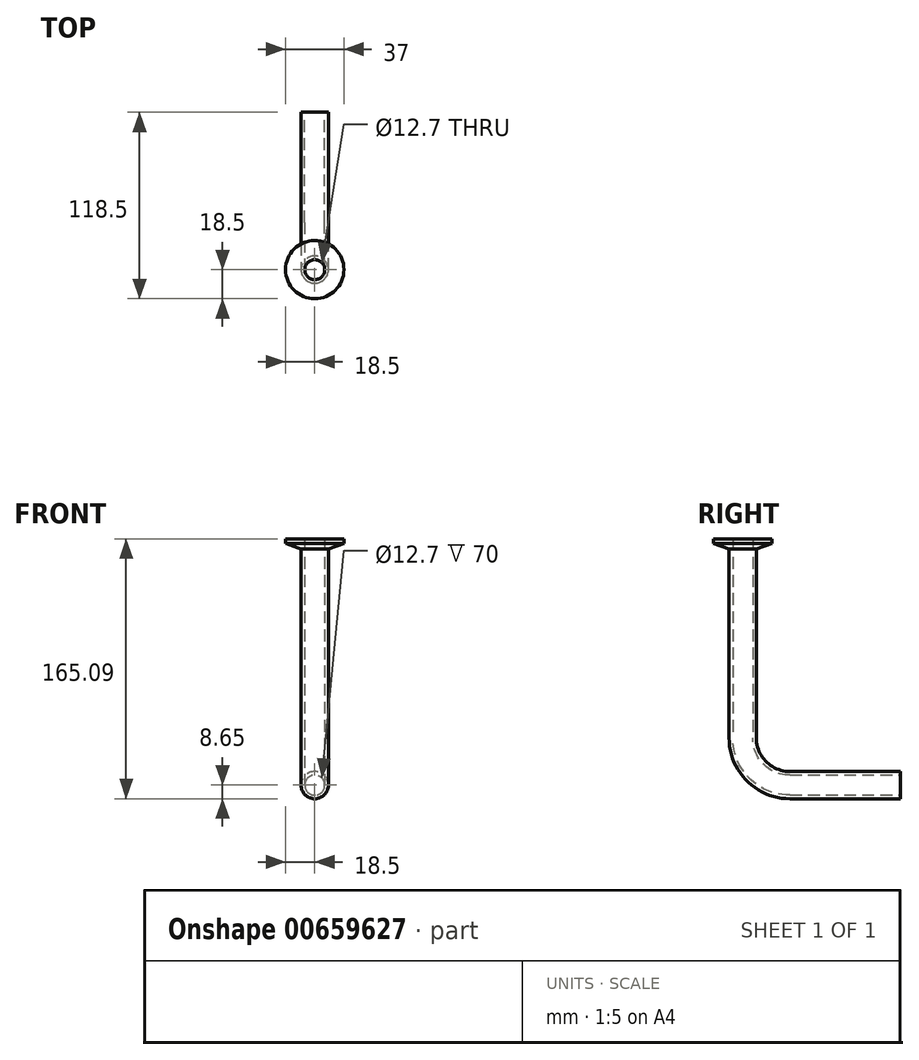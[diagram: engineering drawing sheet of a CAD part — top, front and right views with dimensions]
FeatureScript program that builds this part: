
annotation { "Feature Type Name" : "Feature", "Feature Type Description" : "" }
export const myFeature = defineFeature(function(context is Context, id is Id, definition is map)
    precondition{}
    {
        {
            var Q0;
            Q0=qCreatedBy(makeId("Front.planeOp"),FACE);
            var sketch = newSketch(context, id + "F0", { "sketchPlane" : qUnion([Q0])});
            skLineSegment(sketch, "E0", {"start": v(6.35, 0) * mm, "end": v(6.35, 6.44) * mm});
            skLineSegment(sketch, "E1", {"start": v(6.35, 6.44) * mm, "end": v(18.5, 6.44) * mm});
            skLineSegment(sketch, "E2", {"start": v(18.5, 6.44) * mm, "end": v(18.5, 3.59) * mm});
            skLineSegment(sketch, "E3", {"start": v(18.5, 3.59) * mm, "end": v(8.65, 0) * mm});
            skLineSegment(sketch, "E4", {"start": v(8.65, 0) * mm, "end": v(6.35, 0) * mm});
            skLineSegment(sketch, "E5", {"start": v(0, 0) * mm, "end": v(0, 11.29) * mm, "construction": true});
            skSolve(sketch);
        }
        {
            var Q0;
            Q0=qSketchRegion(id+"F0",true);
            var Q1;
            Q1=sQuery(id+"F0.wireOp",EDGE,"E5");
            revolve(context, id + "F1", {"entities" : qUnion([Q0]), "axis" : qUnion([Q1]), "revolveType" : RevolveType.FULL});
        }
        {
            var Q0;
            Q0=qCreatedBy(makeId("Top.planeOp"),FACE);
            var sketch = newSketch(context, id + "F2", { "sketchPlane" : qUnion([Q0])});
            skCircle(sketch, "E6", {"center": v(0, 0) * mm, "radius": 8.65 * mm});
            skCircle(sketch, "E7", {"center": v(0, 0) * mm, "radius": 6.35 * mm});
            skSolve(sketch);
        }
        {
            var Q0;
            Q0=qCreatedBy(makeId("Right.planeOp"),FACE);
            var sketch = newSketch(context, id + "F3", { "sketchPlane" : qUnion([Q0])});
            skLineSegment(sketch, "E8", {"start": v(0, 0) * mm, "end": v(0, -120) * mm});
            skLineSegment(sketch, "E9", {"start": v(30, -150) * mm, "end": v(100, -150) * mm});
            skPoint(sketch, "E10.visualSharp", {"position": v(0, -150) * mm});
            skArc(sketch, "E10.filletArc", {"start": v(0, -120) * mm, "mid": v(8.79, -141.21) * mm, "end": v(30, -150) * mm});
            skSolve(sketch);
        }
        {
            var Q0;
            Q0=qSketchRegion(id+"F2",true);
            var Q1;
            Q1=qConstructionFilter(qBodyType(qCreatedBy(id+"F3",EDGE),BodyType.WIRE),ConstructionObject.NO);
            sweep(context, id + "F4", {"operationType" : NewBodyOperationType.ADD, "profiles" : qUnion([Q0]), "path" : qUnion([Q1])});
        }
    });
